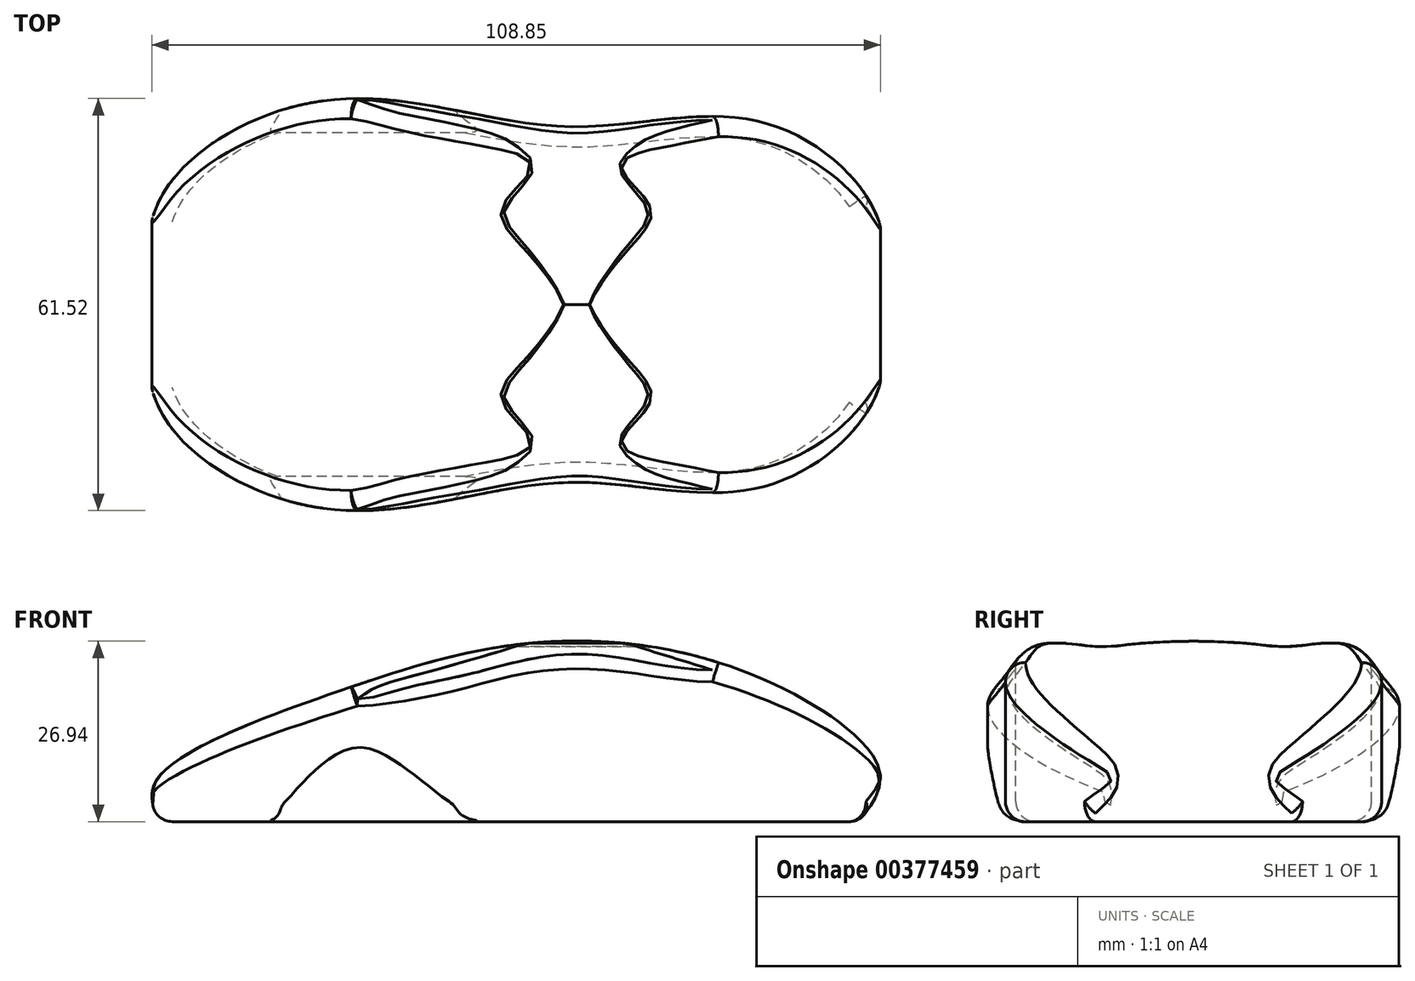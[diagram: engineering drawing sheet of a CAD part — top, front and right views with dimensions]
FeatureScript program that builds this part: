
annotation { "Feature Type Name" : "Feature", "Feature Type Description" : "" }
export const myFeature = defineFeature(function(context is Context, id is Id, definition is map)
    precondition{}
    {
        {
            var Q0;
            Q0=qCreatedBy(makeId("Front.planeOp"),FACE);
            var sketch = newSketch(context, id + "F0", { "sketchPlane" : qUnion([Q0])});
            skLineSegment(sketch, "E0", {"start": v(0, 0) * mm, "end": v(105, 0) * mm});
            skFitSpline(sketch, "E1", {"points": [v(0, 0) * mm, v(0, 6.18) * mm, v(27.7, 19.63) * mm, v(55.31, 26.6) * mm, v(86.9, 22.75) * mm, v(108.02, 7.62) * mm, v(105, 0) * mm], "startDerivative": vector(-14.28, 68.26) * mm, "endDerivative": vector(-46.1, -63.17) * mm});
            skSolve(sketch);
        }
        {
            var Q0;
            Q0 = qSketchRegion(id + "F0", true);
            extrude(context, id + "F1", {"entities" : qUnion([Q0]), "depth" : 31 * mm, "hasSecondDirection" : true, "secondDirectionOppositeDirection" : true, "secondDirectionDepth" : 31 * mm});
        }
        {
            var Q0;
            Q0=qCreatedBy(makeId("Right.planeOp"),FACE);
            var sketch = newSketch(context, id + "F2", { "sketchPlane" : qUnion([Q0])});
            skFitSpline(sketch, "E2", {"points": [v(25.67, 0) * mm, v(29.49, 4.1) * mm, v(30.85, 17.35) * mm, v(28.3, 21.6) * mm, v(23.8, 26.18) * mm, v(14.54, 26.18) * mm, v(0, 26.94) * mm], "startDerivative": vector(63.8, 12.91) * mm, "endDerivative": vector(-136.88, 1.18) * mm});
            skLineSegment(sketch, "E3", {"start": v(25.67, 0) * mm, "end": v(31.7, 0) * mm});
            skLineSegment(sketch, "E4", {"start": v(31.7, 0) * mm, "end": v(31.7, 27.1) * mm});
            skFitSpline(sketch, "E5.MirrorCS", {"points": [v(-25.67, 0) * mm, v(-29.49, 4.1) * mm, v(-30.85, 17.35) * mm, v(-28.3, 21.6) * mm, v(-23.8, 26.18) * mm, v(-14.54, 26.18) * mm, v(0, 26.94) * mm], "startDerivative": vector(-63.8, 12.91) * mm, "endDerivative": vector(136.88, 1.18) * mm});
            skLineSegment(sketch, "E6.MirrorCS", {"start": v(-25.67, 0) * mm, "end": v(-31.7, 0) * mm});
            skLineSegment(sketch, "E7.MirrorCS", {"start": v(-31.7, 0) * mm, "end": v(-31.7, 27.1) * mm});
            skLineSegment(sketch, "E8", {"start": v(31.7, 27.1) * mm, "end": v(0, 27.5) * mm});
            skLineSegment(sketch, "E9", {"start": v(0, 27.5) * mm, "end": v(-31.7, 27.1) * mm});
            skSolve(sketch);
        }
        {
            var Q0;
            Q0 = qSketchRegion(id + "F2", true);
            extrude(context, id + "F3", {"entities" : qUnion([Q0]), "operationType" : NewBodyOperationType.REMOVE, "endBound" : BoundingType.THROUGH_ALL, "depth" : 25 * mm, "hasSecondDirection" : true, "secondDirectionOppositeDirection" : true, "secondDirectionDepth" : 25 * mm});
        }
        {
            var Q0;
            Q0=qCreatedBy(makeId("Top.planeOp"),FACE);
            var sketch = newSketch(context, id + "F4", { "sketchPlane" : qUnion([Q0])});
            skFitSpline(sketch, "E10", {"points": [v(-1.1, 9.13) * mm, v(16.87, 28.41) * mm, v(39.53, 29.95) * mm, v(63.75, 26.55) * mm, v(91.22, 27.03) * mm, v(108.59, 9.66) * mm], "startDerivative": vector(0, 137.15) * mm, "endDerivative": vector(15.3, -114.8) * mm});
            skLineSegment(sketch, "E11", {"start": v(-1.1, 9.13) * mm, "end": v(-1.1, 31.74) * mm});
            skLineSegment(sketch, "E12", {"start": v(-1.1, 31.74) * mm, "end": v(109.64, 31.74) * mm});
            skLineSegment(sketch, "E13", {"start": v(109.64, 31.74) * mm, "end": v(108.59, 9.66) * mm});
            skLineSegment(sketch, "E14.MirrorCS", {"start": v(-1.1, -9.13) * mm, "end": v(-1.1, -31.74) * mm});
            skFitSpline(sketch, "E15.MirrorCS", {"points": [v(-1.1, -9.13) * mm, v(16.87, -28.41) * mm, v(39.53, -29.95) * mm, v(63.75, -26.55) * mm, v(91.22, -27.03) * mm, v(108.59, -9.66) * mm], "startDerivative": vector(0, -137.15) * mm, "endDerivative": vector(15.3, 114.8) * mm});
            skLineSegment(sketch, "E16.MirrorCS", {"start": v(109.64, -31.74) * mm, "end": v(108.59, -9.66) * mm});
            skLineSegment(sketch, "E17.MirrorCS", {"start": v(-1.1, -31.74) * mm, "end": v(109.64, -31.74) * mm});
            skSolve(sketch);
        }
        {
            var Q0;
            Q0 = qSketchRegion(id + "F4", true);
            extrude(context, id + "F5", {"entities" : qUnion([Q0]), "operationType" : NewBodyOperationType.REMOVE, "endBound" : BoundingType.THROUGH_ALL, "oppositeDirection" : true, "depth" : 25 * mm, "hasSecondDirection" : true, "secondDirectionOppositeDirection" : false, "secondDirectionDepth" : 25 * mm});
        }
        {
            var Q0;
            Q0=makeQuery(id+"F3.boolean.opBoolean","SPLIT",FACE,{"disambiguationData":[OD(0.0)],"derivedFrom":makeQuery(id+"F1.opExtrude","SWEPT_FACE",FACE,{"disambiguationData":[OSD([sQuery(id+"F0.wireOp",EDGE,"E1")])]})});
            var Q1;
            Q1=makeQuery(id+"F3.boolean.opBoolean","SPLIT",FACE,{"disambiguationData":[OD(1.0)],"derivedFrom":makeQuery(id+"F1.opExtrude","SWEPT_FACE",FACE,{"disambiguationData":[OSD([sQuery(id+"F0.wireOp",EDGE,"E1")])]})});
            var Q2;
            Q2=makeQuery(id+"F5.boolean.opBoolean","INTERSECT",EDGE,{"disambiguationData":[OD(0.0)],"derivedFrom":[makeQuery(id+"F1.opExtrude","SWEPT_FACE",FACE,{"disambiguationData":[OSD([sQuery(id+"F0.wireOp",EDGE,"E0")])]}),makeQuery(id+"F5.opExtrude","SWEPT_FACE",FACE,{"disambiguationData":[OSD([sQuery(id+"F4.wireOp",EDGE,"E10")])]})]});
            var Q3;
            Q3=makeQuery(id+"F5.boolean.opBoolean","INTERSECT",EDGE,{"disambiguationData":[OD(0.0)],"derivedFrom":[makeQuery(id+"F1.opExtrude","SWEPT_FACE",FACE,{"disambiguationData":[OSD([sQuery(id+"F0.wireOp",EDGE,"E0")])]}),makeQuery(id+"F5.opExtrude","SWEPT_FACE",FACE,{"disambiguationData":[OSD([sQuery(id+"F4.wireOp",EDGE,"E15.MirrorCS")])]})]});
            var Q4;
            Q4=makeQuery(id+"F5.boolean.opBoolean","INTERSECT",EDGE,{"disambiguationData":[OD(1.0)],"derivedFrom":[makeQuery(id+"F1.opExtrude","SWEPT_FACE",FACE,{"disambiguationData":[OSD([sQuery(id+"F0.wireOp",EDGE,"E0")])]}),makeQuery(id+"F5.opExtrude","SWEPT_FACE",FACE,{"disambiguationData":[OSD([sQuery(id+"F4.wireOp",EDGE,"E15.MirrorCS")])]})]});
            var Q5;
            Q5=makeQuery(id+"F5.boolean.opBoolean","INTERSECT",EDGE,{"disambiguationData":[OD(1.0)],"derivedFrom":[makeQuery(id+"F1.opExtrude","SWEPT_FACE",FACE,{"disambiguationData":[OSD([sQuery(id+"F0.wireOp",EDGE,"E0")])]}),makeQuery(id+"F5.opExtrude","SWEPT_FACE",FACE,{"disambiguationData":[OSD([sQuery(id+"F4.wireOp",EDGE,"E10")])]})]});
            var Q6;
            Q6=makeQuery(id+"F5.boolean.opBoolean","INTERSECT",EDGE,{"derivedFrom":[makeQuery(id+"F3.boolean.opBoolean","COPY",FACE,{"disambiguationData":[TD([makeQuery(id+"F3.opExtrude","SWEPT_FACE",FACE,{"disambiguationData":[OSD([sQuery(id+"F2.wireOp",EDGE,"E2")])]})])],"derivedFrom":makeQuery(id+"F3.opExtrude","SWEPT_FACE",FACE,{"disambiguationData":[OSD([sQuery(id+"F2.wireOp",EDGE,"E5.MirrorCS")])]})}),makeQuery(id+"F5.opExtrude","SWEPT_FACE",FACE,{"disambiguationData":[OSD([sQuery(id+"F4.wireOp",EDGE,"E15.MirrorCS")])]})]});
            var Q7;
            Q7=makeQuery(id+"F5.boolean.opBoolean","INTERSECT",EDGE,{"derivedFrom":[makeQuery(id+"F3.boolean.opBoolean","COPY",FACE,{"disambiguationData":[TD([makeQuery(id+"F3.opExtrude","SWEPT_FACE",FACE,{"disambiguationData":[OSD([sQuery(id+"F2.wireOp",EDGE,"E5.MirrorCS")])]})])],"derivedFrom":makeQuery(id+"F3.opExtrude","SWEPT_FACE",FACE,{"disambiguationData":[OSD([sQuery(id+"F2.wireOp",EDGE,"E2")])]})}),makeQuery(id+"F5.opExtrude","SWEPT_FACE",FACE,{"disambiguationData":[OSD([sQuery(id+"F4.wireOp",EDGE,"E10")])]})]});
            fillet(context, id + "F6", {"entities" : qUnion([Q0, Q1, Q2, Q3, Q4, Q5, Q6, Q7]), "radius" : 3 * mm, "tangentPropagation" : true, "allowEdgeOverflow" : false});
        }
    });
